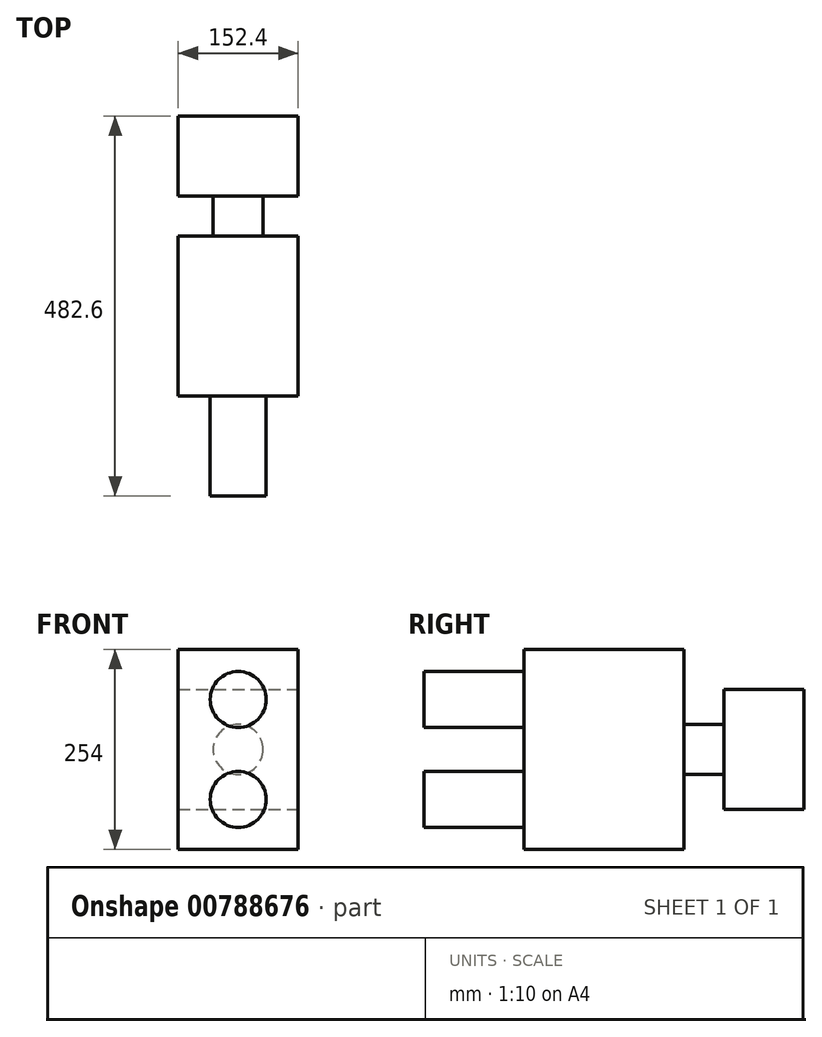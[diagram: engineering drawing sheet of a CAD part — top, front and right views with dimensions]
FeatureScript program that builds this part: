
annotation { "Feature Type Name" : "Feature", "Feature Type Description" : "" }
export const myFeature = defineFeature(function(context is Context, id is Id, definition is map)
    precondition{}
    {
        {
            var Q0;
            Q0=qCreatedBy(makeId("Front.planeOp"),FACE);
            var sketch = newSketch(context, id + "F0", { "sketchPlane" : qUnion([Q0])});
            skLineSegment(sketch, "E0.bottom", {"start": v(-76.2, 76.2) * mm, "end": v(76.2, 76.2) * mm});
            skLineSegment(sketch, "E0.top", {"start": v(-76.2, -76.2) * mm, "end": v(76.2, -76.2) * mm});
            skLineSegment(sketch, "E0.left", {"start": v(-76.2, 76.2) * mm, "end": v(-76.2, -76.2) * mm});
            skLineSegment(sketch, "E0.right", {"start": v(76.2, 76.2) * mm, "end": v(76.2, -76.2) * mm});
            skPoint(sketch, "E0.middle", {"position": v(0, 0) * mm});
            skSolve(sketch);
        }
        {
            var Q0;
            Q0 = qSketchRegion(id + "F0", true);
            extrude(context, id + "F1", {"entities" : qUnion([Q0]), "depth" : 101.6 * mm, "offsetDistance" : 25.4 * mm});
        }
        {
            var Q0;
            Q0=makeQuery(id+"F1.opExtrude","CAP_FACE",FACE,{"disambiguationData":[OSD([sQuery(id+"F0.wireOp",EDGE,"E0.bottom"),sQuery(id+"F0.wireOp",EDGE,"E0.top"),sQuery(id+"F0.wireOp",EDGE,"E0.left"),sQuery(id+"F0.wireOp",EDGE,"E0.right")])],"isStart":false});
            var sketch = newSketch(context, id + "F2", { "sketchPlane" : qUnion([Q0])});
            skCircle(sketch, "E1", {"center": v(0, 0) * mm, "radius": 31.75 * mm});
            skSolve(sketch);
        }
        {
            var Q0;
            Q0 = qSketchRegion(id + "F2", true);
            extrude(context, id + "F3", {"entities" : qUnion([Q0]), "operationType" : NewBodyOperationType.ADD, "depth" : 50.8 * mm, "offsetDistance" : 25.4 * mm});
        }
        {
            var Q0;
            Q0=makeQuery(id+"F3.opExtrude","CAP_FACE",FACE,{"disambiguationData":[OSD([sQuery(id+"F2.wireOp",EDGE,"E1")])],"isStart":false});
            var sketch = newSketch(context, id + "F4", { "sketchPlane" : qUnion([Q0])});
            skLineSegment(sketch, "E2.bottom", {"start": v(-76.2, -127) * mm, "end": v(76.2, -127) * mm});
            skLineSegment(sketch, "E2.top", {"start": v(-76.2, 127) * mm, "end": v(76.2, 127) * mm});
            skLineSegment(sketch, "E2.left", {"start": v(-76.2, -127) * mm, "end": v(-76.2, 127) * mm});
            skLineSegment(sketch, "E2.right", {"start": v(76.2, -127) * mm, "end": v(76.2, 127) * mm});
            skPoint(sketch, "E2.middle", {"position": v(0, 0) * mm});
            skSolve(sketch);
        }
        {
            var Q0;
            Q0 = qSketchRegion(id + "F4", true);
            extrude(context, id + "F5", {"entities" : qUnion([Q0]), "operationType" : NewBodyOperationType.ADD, "depth" : 203.2 * mm, "offsetDistance" : 25.4 * mm});
        }
        {
            var Q0;
            Q0=makeQuery(id+"F5.opExtrude","CAP_FACE",FACE,{"disambiguationData":[OSD([sQuery(id+"F4.wireOp",EDGE,"E2.bottom"),sQuery(id+"F4.wireOp",EDGE,"E2.top"),sQuery(id+"F4.wireOp",EDGE,"E2.left"),sQuery(id+"F4.wireOp",EDGE,"E2.right")])],"isStart":false});
            var sketch = newSketch(context, id + "F6", { "sketchPlane" : qUnion([Q0])});
            skLineSegment(sketch, "E3", {"start": v(0, 0) * mm, "end": v(0, 127) * mm, "construction": true});
            skLineSegment(sketch, "E4", {"start": v(0, 0) * mm, "end": v(0, -127) * mm, "construction": true});
            skCircle(sketch, "E5", {"center": v(0, -63.5) * mm, "radius": 35.56 * mm});
            skCircle(sketch, "E6.MirrorC", {"center": v(0, 63.5) * mm, "radius": 35.56 * mm});
            skSolve(sketch);
        }
        {
            var Q0;
            Q0 = qSketchRegion(id + "F6", true);
            extrude(context, id + "F7", {"entities" : qUnion([Q0]), "operationType" : NewBodyOperationType.ADD, "depth" : 127 * mm, "offsetDistance" : 25.4 * mm});
        }
    });
